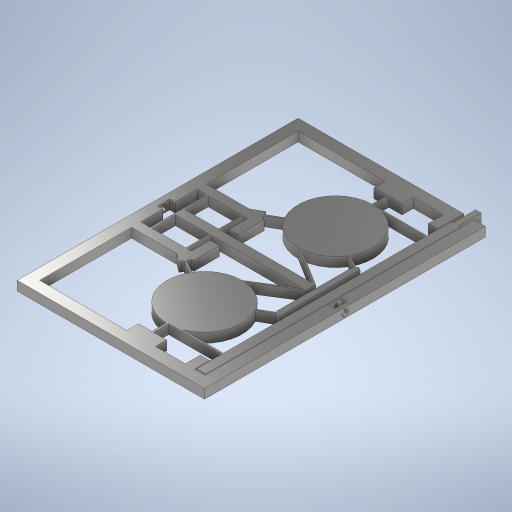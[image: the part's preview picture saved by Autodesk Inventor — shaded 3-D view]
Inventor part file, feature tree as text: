
AUTODESK INVENTOR PART (.ipt)
format: ipt  version: 2023 (Build 270158000, 158)  size: 664,576 bytes
history: native  units: mm
features: extrude x6, sketch x6, other x1
ambient origin geometry x8: Origin, YZ Plane, XZ Plane, XY Plane, X Axis, Y Axis, Z Axis, Center Point
bodies: Solid1 (feature_tree)
feature tree (13):
  other  "<userpath>\OneDrive\ClawdDrive\Objet3D\IminaProbe\Settings.xlsx"
  extrude  "Extrusion1"  Depth=100.0mm
  extrude  "Extrusion6"  TaperAngle=0.0deg  [1 undecoded]
  extrude  "Extrusion7"  Depth=1.0mm
  extrude  "Extrusion9"  Depth=1.0mm
  extrude  "Extrusion10"  Depth=50.0mm
  extrude  "Extrusion11"  Depth=6.0mm
  sketch  "Sketch1"  dims[d0=150.0mm d1=100.0mm]
  sketch  "Sketch6"  dims[d2=5.0mm d3=0.0mm]
  sketch  "Sketch7"  dims[d14=1.0mm d16=1.0mm]
  sketch  "Sketch9"  dims[d19=1.0mm d23=52.849025mm d24=57.849025mm]
  sketch  "Sketch10"  dims[d25=67.849025mm]
  sketch  "Sketch11"  dims[d31=45.0deg d32=45.0deg d33=45.0deg d34=45.0deg d40=45.0deg d45=45.0deg d46=45.0deg d47=45.0deg d80=50.0mm d81=50.0mm d89=6.0mm d90=6.0mm d91=6.0mm d92=6.0mm d93=5.0mm d94=136.0mm d95=1.0mm d96=8.0mm d97=5.0mm d98=5.5mm d100=5.0mm d101=5.5mm d103=3.0mm d104=20.0mm d105=1.0mm d106=0.25mm d112=40.0mm d113=40.0mm d116=1.0mm d117=1.0mm d118=1.0mm d119=1.0mm d120=11.34464mm d121=11.34464mm d124=25.0mm d125=30.0mm d126=5.0mm d127=5.0mm d128=40.0mm d129=55.0mm d130=20.0mm d131=20.0mm d132=20.0mm d133=20.0mm d134=1.0mm d135=1.0mm d138=10.12291mm d139=10.12291mm d140=10.12291mm d141=10.12291mm d142=15.0mm d145=8.0mm d150=1.0mm d151=1.0mm d152=5.0mm d153=2.0mm d154=2.0mm d155=5.0mm d156=5.0mm d157=15.0mm d158=15.0mm d159=40.0mm d160=40.0mm d161=0.0mm d162=5.0mm d165=30.0mm d167=360.0deg d169=30.0deg d171=2.0mm d172=5.0mm d173=3.0mm d175=1.5mm d176=1.0mm d177=0.5mm d178=0.5mm d179=28.0mm d180=0.0mm d181=28.0mm d182=30.0mm d184=360.0deg d186=30.0deg d187=3.0mm d188=1.5mm d189=1.0mm d190=0.5mm d192=0.0mm d193=0.0mm d194=5.0mm d195=2.5mm d196=0.5mm d199=0.5mm d200=8.0mm d201=8.0mm d202=8.0mm d203=8.0mm d204=0.5mm d205=0.5mm d206=5.0mm d207=2.5mm d209=5.0mm d211=2.5mm d212=0.5mm d213=0.5mm d214=8.0mm d215=20.0mm d216=20.0mm d217=20.0mm d218=20.0mm d219=5.0mm d220=0.5mm d221=0.5mm d222=2.5mm d223=5.0mm d224=5.0mm d225=5.0mm d226=5.0mm d227=1.0mm d228=1.0mm d229=8.0mm d230=1.0mm d231=1.0mm d233=2.0mm d234=3.0mm d235=3.0mm d237=3.0mm d238=3.0mm d239=10.0mm d240=0.0mm d241=6.5mm d242=6.5mm d244=3.25mm d245=3.25mm d246=6.5mm d247=6.5mm d248=3.25mm d249=3.25mm d250=6.5mm d251=0.75mm d252=0.0mm d253=5.0mm d254=5.0mm d255=0.0mm d259=10.0mm d265=3.0mm d266=6.5mm d267=6.0mm d268=1.0mm d269=150.0mm d270=71.75mm d271=10.0mm d272=0.0mm d273=75.0mm d274=3.5mm d275=2.5mm d276=5.0mm d277=12.0mm d278=0.0mm d279=5.0mm d280=2.5mm d281=3.5mm d282=75.0mm d283=8.0mm d284=0.0mm d285=0.5mm d286=0.5mm d287=0.0mm]
note: 1 required parameter value undecoded (feature->parameter linkage not recoverable at this tier; creation-order binding heuristic only, values carry confidence <= 0.55)
